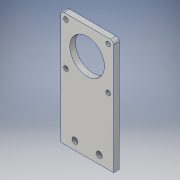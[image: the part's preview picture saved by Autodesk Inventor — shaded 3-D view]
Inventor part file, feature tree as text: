
AUTODESK INVENTOR PART (.ipt)
format: ipt  version: 2016 (Build 200138000, 138)  size: 145,920 bytes
history: native  units: in
note: dims shown in document units (in); Inventor stores cm internally (conversion verified against a paired STEP export)
features: extrude x4, sketch x4, fillet x1
ambient origin geometry x8: Origin, YZ Plane, XZ Plane, XY Plane, X Axis, Y Axis, Z Axis, Center Point
bodies: Solid1 (feature_tree)
feature tree (9):
  extrude  "Extrusion1"  Depth=5.0in
  extrude  "Extrusion2"  Depth=0.25in
  extrude  "Extrusion3"  Depth=0.25in TaperAngle=0.0deg
  fillet  "Fillet1"  Radius=0.205in
  extrude  "Extrusion4"  Depth=0.142in
  sketch  "Sketch1"  dims[d0=2.318in d1=5.0in]
  sketch  "Sketch2"  dims[d2=0.25in d3=0.0in d4=1.52in]
  sketch  "Sketch3"  dims[d5=1.159in d8=0.25in d9=0.0in d10=0.205in]
  sketch  "Sketch4"  dims[d11=0.229in d12=0.229in d13=0.7874in d15=1.856in d16=0.7874in d18=1.856in d21=0.25in d22=0.0in d23=0.142in d24=0.26in d25=0.26in d26=0.375in d27=0.375in d28=0.625in d29=0.625in d30=1.0in d31=0.0in]
